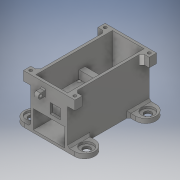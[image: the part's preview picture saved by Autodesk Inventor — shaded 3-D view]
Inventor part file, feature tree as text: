
AUTODESK INVENTOR PART (.ipt)
format: ipt  version: 2018 (Build 220112000, 112)  size: 1,288,704 bytes
history: native  units: in
note: dims shown in document units (in); Inventor stores cm internally (conversion verified against a paired STEP export)
features: sketch x33, extrude x30, move_body x15, direct_edit x10, chamfer x6, fillet x5, thicken_offset x3, delete_face x3, projected_geometry x1
ambient origin geometry x8: Origin, YZ Plane, XZ Plane, XY Plane, X Axis, Y Axis, Z Axis, Center Point
bodies: Solid1 (feature_tree)
feature tree (106):
  extrude  "Extrusion1"  Depth=0.125in
  extrude  "Extrusion2"  Depth=0.9in TaperAngle=0.0deg
  extrude  "Extrusion3"  Depth=2.0in
  extrude  "Extrusion4"  Depth=0.0625in
  sketch  "Sketch6"  dims[d11=0.5in d13=0.55in]
  extrude  "Extrusion6"  Depth=0.55in
  extrude  "Extrusion7"  Depth=0.725in
  extrude  "Extrusion8"  Depth=0.09in
  extrude  "Extrusion9"  Depth=0.125in
  extrude  "Extrusion10"  Depth=0.125in TaperAngle=0.0deg
  extrude  "Extrusion11"  Depth=0.7in
  extrude  "Extrusion12"  Depth=0.5in
  sketch  "Sketch16"  dims[d38=0.05in]
  extrude  "Extrusion13"  Depth=0.5in
  sketch  "Sketch18"  dims[d40=0.45in]
  fillet  "Fillet1"  Radius=0.05in
  chamfer  "Chamfer1"  Distance=0.36in
  chamfer  "Chamfer2"  Distance=0.25in
  extrude  "Extrusion14"  Depth=0.05in
  extrude  "Extrusion15"  Depth=0.35in
  extrude  "Extrusion16"  Depth=0.25in
  fillet  "Fillet2"  Radius=0.25in
  extrude  "Extrusion17"  Depth=0.1in
  chamfer  "Chamfer3"  Distance=0.125in Angle=45.0deg
  extrude  "Extrusion18"  Depth=0.125in
  extrude  "Extrusion19"  Depth=0.4in TaperAngle=0.0deg
  extrude  "Extrusion20"  Depth=0.05in
  extrude  "Extrusion21"  Depth=0.1in
  fillet  "Fillet3"  Radius=0.275in
  fillet  "Fillet4"  Radius=0.36in
  extrude  "Extrusion22"  Depth=0.225in
  extrude  "Extrusion23"  Depth=1.0in
  chamfer  "Chamfer4"  Distance=0.146in
  chamfer  "Chamfer5"  Distance=0.26in
  extrude  "Extrusion24"  Depth=0.123in
  extrude  "Extrusion25"  Depth=1.0in
  extrude  "Extrusion28"  Depth=1.0in
  extrude  "Extrusion29"  Depth=1.0in TaperAngle=0.0deg
  extrude  "Extrusion30"  Depth=0.125in TaperAngle=45.0deg
  extrude  "Extrusion31"  Depth=0.45in
  thicken_offset  "Thicken1"
  thicken_offset  "Thicken2"
  thicken_offset  "Thicken3"
  direct_edit  "Direct Edit1"
  direct_edit  "Direct Edit2"
  direct_edit  "Direct Edit3"
  direct_edit  "Direct Edit4"
  extrude  "Extrusion32"  Depth=1.0in TaperAngle=0.0deg
  fillet  "Fillet5"  Radius=0.125in
  chamfer  "Chamfer7"  Distance=0.125in
  direct_edit  "Direct Edit5"
  direct_edit  "Direct Edit6"
  direct_edit  "Direct Edit7"
  direct_edit  "Direct Edit8"
  delete_face  "Delete Face1"
  direct_edit  "Direct Edit9"
  delete_face  "Delete Face2"
  direct_edit  "Direct Edit10"
  delete_face  "Delete Face3"
  extrude  "Extrusion33"  Depth=1.0in
  sketch  "Sketch1"  dims[d0=0.125in d1=1.24in]
  sketch  "Sketch2"  dims[d2=0.9in d3=2.2in d4=0.0in]
  sketch  "Sketch3"  dims[d5=0.125in d6=0.0in d7=2.0in]
  sketch  "Sketch4"  dims[d8=0.125in d9=0.0in d10=0.0625in]
  sketch  "Sketch8"  dims[d14=0.125in d15=0.0in d16=0.725in]
  sketch  "Sketch10"  dims[d17=2.06in d21=0.09in]
  sketch  "Sketch11"  dims[d22=0.4in d23=0.0in d24=0.125in]
  sketch  "Sketch12"  dims[d25=1.475in d26=0.0in d27=0.125in d28=0.0in]
  sketch  "Sketch13"  dims[d29=0.6in d30=0.7in]
  sketch  "Sketch14"  dims[d31=0.5in d32=0.0in d33=0.1603in]
  sketch  "Sketch15"  dims[d34=0.5in d35=0.0in d36=0.146in d37=0.05in]
  sketch  "Sketch17"  dims[d39=0.1in]
  sketch  "Sketch19"  dims[d41=1.0in d42=0.36in d43=0.0in]
  sketch  "Sketch20"  dims[d44=0.225in]
  sketch  "Sketch21"  dims[d45=0.146in d46=0.25in d47=0.0in]
  sketch  "Sketch22"  dims[d49=0.05in d50=0.0in d51=0.05in]
  sketch  "Sketch24"  dims[d52=0.05in d53=0.35in]
  sketch  "Sketch25"  dims[d54=0.02in d55=0.02in d56=0.25in]
  sketch  "Sketch26"  dims[d57=0.25in d58=0.1in]
  sketch  "Sketch27"  dims[d59=0.0in]
  sketch  "Sketch28"  dims[d60=0.35in]
  sketch  "Sketch29"  dims[d61=0.346in]
  sketch  "Sketch30"  dims[d62=0.425in]
  sketch  "Sketch31"  dims[d63=0.9in]
  sketch  "Sketch34"  dims[d64=0.123in]
  sketch  "Sketch35"  dims[d65=0.123in d66=0.05in d67=0.125in d68=45.0deg]
  sketch  "Sketch36"  dims[d69=0.05in d70=0.125in d71=45.0deg d72=0.01in]
  sketch  "Sketch37"  dims[d73=0.4in d74=0.05in d75=0.0in]
  projected_geometry  "Projected Loop1"
  sketch  "Sketch38"  dims[d76=0.146in d77=0.05in]
  sketch  "Sketch39"  dims[d78=0.05in d80=0.1in d81=0.275in d82=0.36in d83=0.0in d84=0.225in d85=0.01in d86=0.146in d87=0.26in d88=0.0in d89=0.123in d90=0.05in d91=0.05in d92=0.05in d93=0.0in d94=0.05in d95=0.125in d96=45.0deg d97=0.45in d98=0.05in d99=0.0in d100=0.125in d101=0.0in d102=0.125in d103=0.0in d104=1.0in d105=1.0in d106=1.0in d107=0.912in d108=0.912in d109=0.912in d110=0.912in d111=0.21in d112=0.0in d113=0.5in d114=0.63in d115=0.63in d116=0.63in d117=0.63in d118=0.437in d119=0.437in d120=0.437in d121=0.437in d122=0.1in d123=0.0in d124=0.344in d125=0.344in d126=0.344in d127=0.344in d128=0.1in d129=0.0in d130=0.1in d131=0.125in d132=45.0deg d133=0.05in d134=0.125in d135=45.0deg d139=0.312in d140=0.3603in d141=0.3603in d142=0.3603in d143=0.3603in d144=0.3603in d145=0.45in d146=0.0in d147=0.146in d148=0.146in d149=0.146in d150=0.146in d151=0.5in d152=0.0in d163=1.0in d164=0.0in d165=0.35in d166=1.5in d168=0.3in d169=1.0in d170=0.0in d171=0.05in d172=0.3in d173=0.0in d174=0.05in d175=0.0in d176=0.1in d177=0.1in d178=0.1in d179=0.1in d180=0.1in d181=0.1in d182=0.0in d183=0.0in d184=0.1in d185=0.0in d186=0.0in d187=-0.1in d188=0.0in d189=0.0in d190=-0.05in d191=0.5in d192=0.0in d193=0.0in d194=0.05in d195=0.937in d196=0.937in d197=0.937in d198=0.937in d199=0.375in d200=0.0in d201=0.5in d202=0.125in d203=0.125in d204=45.0deg d205=0.0in d206=0.0in d207=-0.175in d208=0.0in d209=0.0in d210=0.35in d211=0.0in d212=0.0in d213=0.105in d214=0.0in d215=0.0in d216=0.105in d217=0.0in d218=0.0in d219=0.1in d220=0.0in d221=0.0in d222=0.1in d223=0.0in d224=0.0in d225=0.02in d226=0.0in d227=0.0in d228=0.09in d229=0.0in d230=0.0in d231=0.02in d232=0.0in d233=0.0in d234=0.09in d235=0.3in d236=0.0in d237=0.0in d238=0.16in d239=1.0in d240=0.0in]
  move_body  "Move1"
  move_body  "Move2"
  move_body  "Move3"
  move_body  "Move4"
  move_body  "Move5"
  move_body  "Move6"
  move_body  "Move7"
  move_body  "Move8"
  move_body  "Move9"
  move_body  "Move10"
  move_body  "Move11"
  move_body  "Move12"
  move_body  "Move13"
  move_body  "Move14"
  move_body  "Move15"
